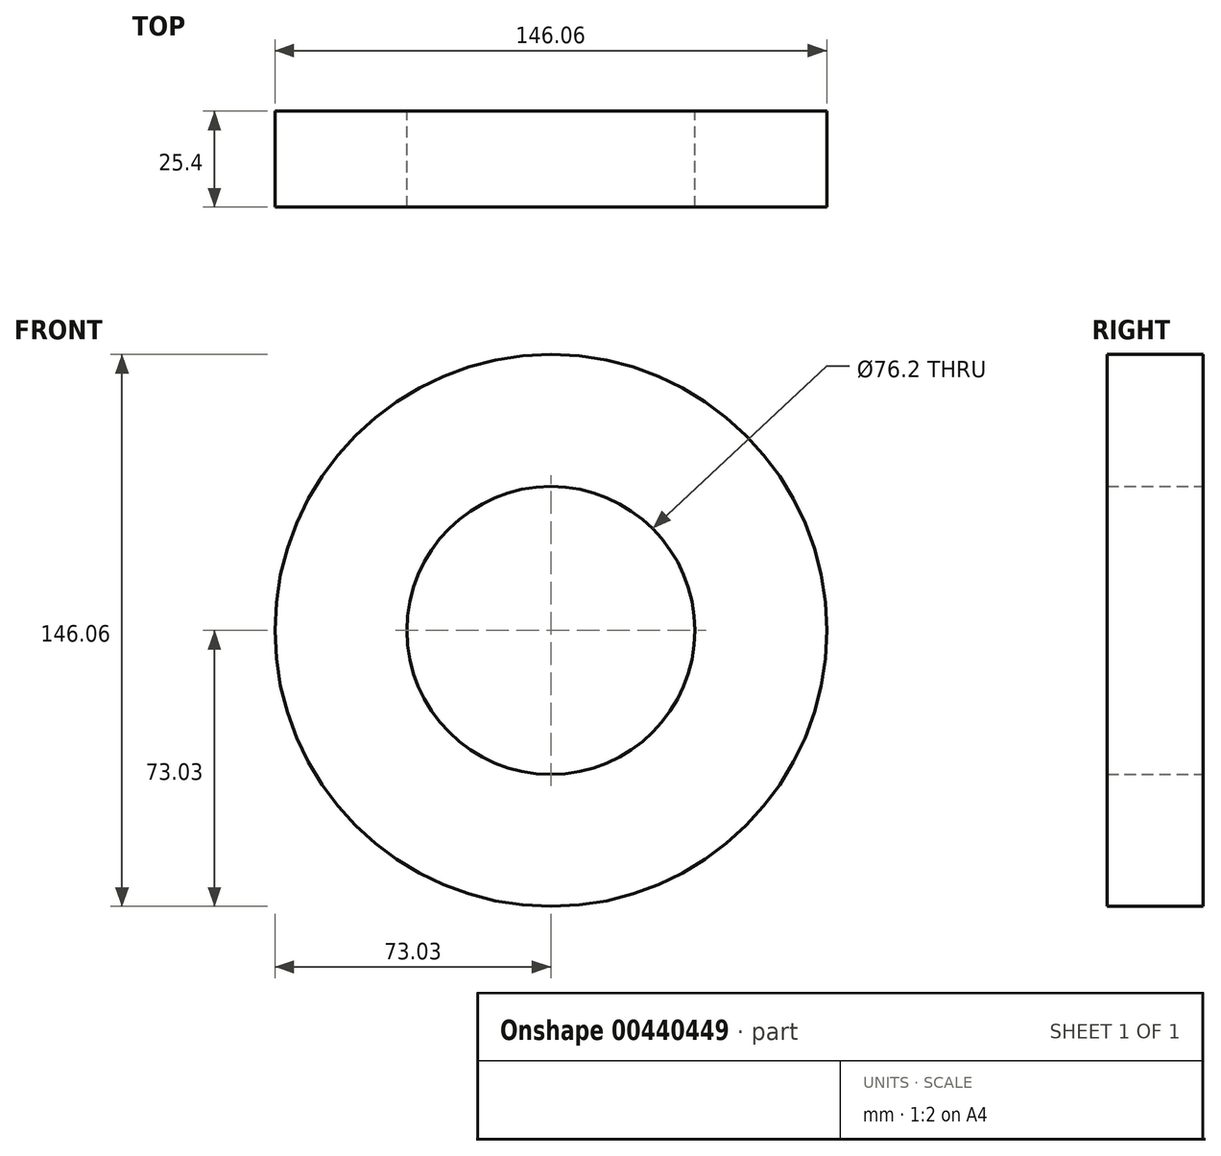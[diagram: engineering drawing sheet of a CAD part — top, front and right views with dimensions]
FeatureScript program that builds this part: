
annotation { "Feature Type Name" : "Feature", "Feature Type Description" : "" }
export const myFeature = defineFeature(function(context is Context, id is Id, definition is map)
    precondition{}
    {
        {
            var Q0;
            Q0=qCreatedBy(makeId("Front.planeOp"),FACE);
            var sketch = newSketch(context, id + "F0", { "sketchPlane" : qUnion([Q0])});
            skCircle(sketch, "E0", {"center": v(0, 0) * mm, "radius": 38.1 * mm});
            skCircle(sketch, "E1", {"center": v(0, 0) * mm, "radius": 73.03 * mm});
            skSolve(sketch);
        }
        {
            var Q0;
            Q0=makeQuery(id+"F0.imprint","IMPRINT",FACE,{"disambiguationData":[TD([[makeQuery(id+"F0.imprint","IMPRINT",EDGE,{"derivedFrom":sQuery(id+"F0.wireOp",EDGE,"E0")}),-1.0]])]});
            extrude(context, id + "F1", {"entities" : qUnion([Q0]), "depth" : 25.4 * mm});
        }
    });
